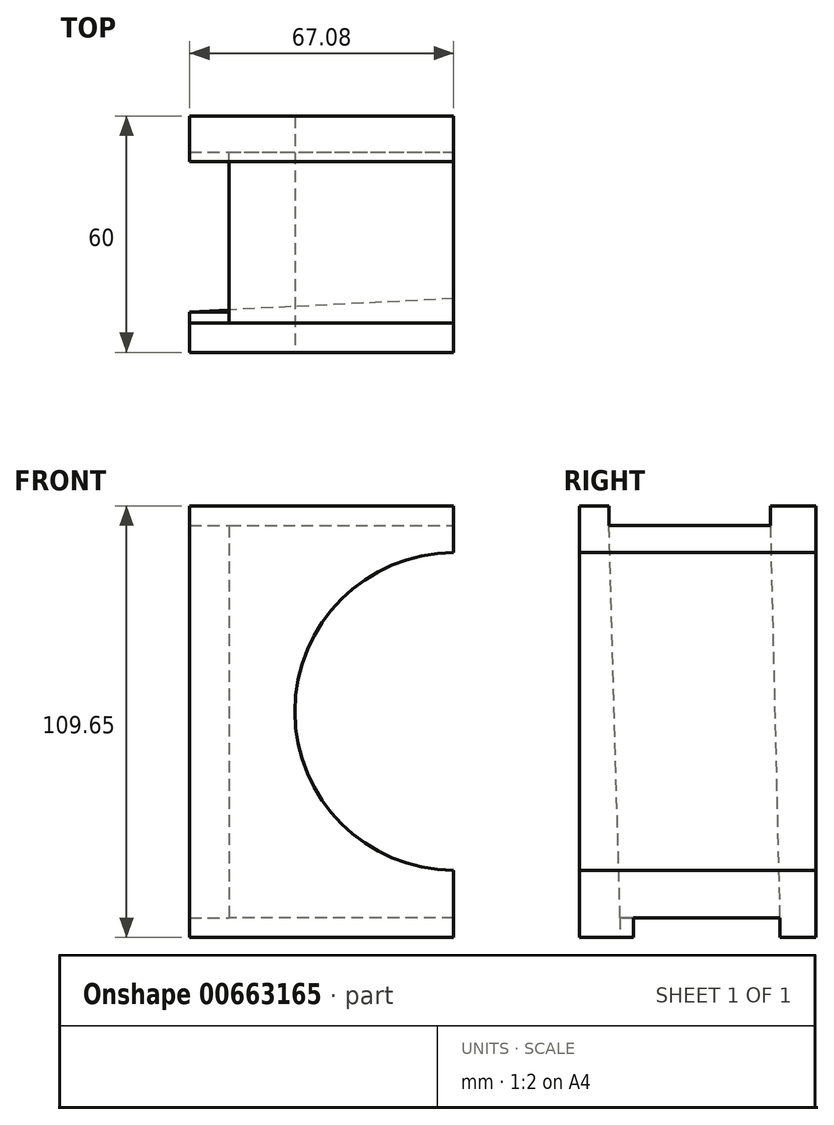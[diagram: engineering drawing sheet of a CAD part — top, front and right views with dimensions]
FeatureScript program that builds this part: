
annotation { "Feature Type Name" : "Feature", "Feature Type Description" : "" }
export const myFeature = defineFeature(function(context is Context, id is Id, definition is map)
    precondition{}
    {
        {
            var Q0;
            Q0=qCreatedBy(makeId("Front.planeOp"),FACE);
            var sketch = newSketch(context, id + "F0", { "sketchPlane" : qUnion([Q0])});
            skLineSegment(sketch, "E0", {"start": v(-33.77, 50.02) * mm, "end": v(-33.77, -59.63) * mm});
            skLineSegment(sketch, "E1", {"start": v(-33.77, -59.63) * mm, "end": v(33.31, -59.63) * mm});
            skLineSegment(sketch, "E2", {"start": v(33.31, -59.63) * mm, "end": v(33.31, 50.02) * mm});
            skLineSegment(sketch, "E3", {"start": v(33.31, 50.02) * mm, "end": v(-33.77, 50.02) * mm});
            skSolve(sketch);
        }
        {
            var Q0;
            Q0 = qSketchRegion(id + "F0", true);
            extrude(context, id + "F1", {"entities" : qUnion([Q0]), "depth" : 60 * mm, "offsetDistance" : 25 * mm});
        }
        {
            var Q0;
            Q0=makeQuery(id+"F1.opExtrude","CAP_FACE",FACE,{"disambiguationData":[OSD([sQuery(id+"F0.wireOp",EDGE,"E0"),sQuery(id+"F0.wireOp",EDGE,"E1"),sQuery(id+"F0.wireOp",EDGE,"E2"),sQuery(id+"F0.wireOp",EDGE,"E3")])],"isStart":false});
            var sketch = newSketch(context, id + "F2", { "sketchPlane" : qUnion([Q0])});
            skCircle(sketch, "E4", {"center": v(33.31, -2.24) * mm, "radius": 40.33 * mm});
            skSolve(sketch);
        }
        {
            var Q0;
            Q0 = qSketchRegion(id + "F2", true);
            extrude(context, id + "F3", {"entities" : qUnion([Q0]), "operationType" : NewBodyOperationType.REMOVE, "oppositeDirection" : true, "depth" : 60 * mm, "offsetDistance" : 25 * mm});
        }
        {
            var Q0;
            Q0=makeQuery(id+"F1.opExtrude","SWEPT_FACE",FACE,{"disambiguationData":[OSD([sQuery(id+"F0.wireOp",EDGE,"E3")])]});
            var sketch = newSketch(context, id + "F4", { "sketchPlane" : qUnion([Q0])});
            skLineSegment(sketch, "E5", {"start": v(-33.77, -52.54) * mm, "end": v(33.31, -52.54) * mm});
            skLineSegment(sketch, "E6", {"start": v(33.31, -52.54) * mm, "end": v(33.31, -11.56) * mm});
            skLineSegment(sketch, "E7", {"start": v(33.31, -11.56) * mm, "end": v(-33.77, -11.56) * mm});
            skLineSegment(sketch, "E8", {"start": v(-33.77, -11.56) * mm, "end": v(-33.77, -52.54) * mm});
            skSolve(sketch);
        }
        {
            var Q0;
            Q0 = qSketchRegion(id + "F4", true);
            extrude(context, id + "F5", {"entities" : qUnion([Q0]), "operationType" : NewBodyOperationType.REMOVE, "oppositeDirection" : true, "depth" : 5 * mm, "offsetDistance" : 25 * mm});
        }
        {
            var Q0;
            Q0=makeQuery(id+"F1.opExtrude","SWEPT_FACE",FACE,{"disambiguationData":[OSD([sQuery(id+"F0.wireOp",EDGE,"E1")])]});
            var sketch = newSketch(context, id + "F6", { "sketchPlane" : qUnion([Q0])});
            skLineSegment(sketch, "E9", {"start": v(-33.77, 9.18) * mm, "end": v(33.31, 9.18) * mm});
            skLineSegment(sketch, "E10", {"start": v(33.31, 9.18) * mm, "end": v(33.31, 46.38) * mm});
            skLineSegment(sketch, "E11", {"start": v(33.31, 46.38) * mm, "end": v(-33.77, 49.7) * mm});
            skLineSegment(sketch, "E12", {"start": v(-33.77, 49.7) * mm, "end": v(-33.77, 9.18) * mm});
            skSolve(sketch);
        }
        {
            var Q0;
            Q0 = qSketchRegion(id + "F6", true);
            extrude(context, id + "F7", {"entities" : qUnion([Q0]), "operationType" : NewBodyOperationType.REMOVE, "oppositeDirection" : true, "depth" : 5 * mm, "offsetDistance" : 25 * mm});
        }
        {
            var Q0;
            Q0=makeQuery(id+"F1.opExtrude","SWEPT_FACE",FACE,{"disambiguationData":[OSD([sQuery(id+"F0.wireOp",EDGE,"E0")])]});
            var sketch = newSketch(context, id + "F8", { "sketchPlane" : qUnion([Q0])});
            skLineSegment(sketch, "E13", {"start": v(11.56, 45.02) * mm, "end": v(9.18, -54.63) * mm});
            skLineSegment(sketch, "E14", {"start": v(9.18, -54.63) * mm, "end": v(49.7, -54.63) * mm});
            skLineSegment(sketch, "E15", {"start": v(49.7, -54.63) * mm, "end": v(52.54, 45.02) * mm});
            skLineSegment(sketch, "E16", {"start": v(52.54, 45.02) * mm, "end": v(11.56, 45.02) * mm});
            skSolve(sketch);
        }
        {
            var Q0;
            Q0 = qSketchRegion(id + "F8", true);
            extrude(context, id + "F9", {"entities" : qUnion([Q0]), "operationType" : NewBodyOperationType.REMOVE, "oppositeDirection" : true, "depth" : 10 * mm, "offsetDistance" : 25 * mm});
        }
    });
